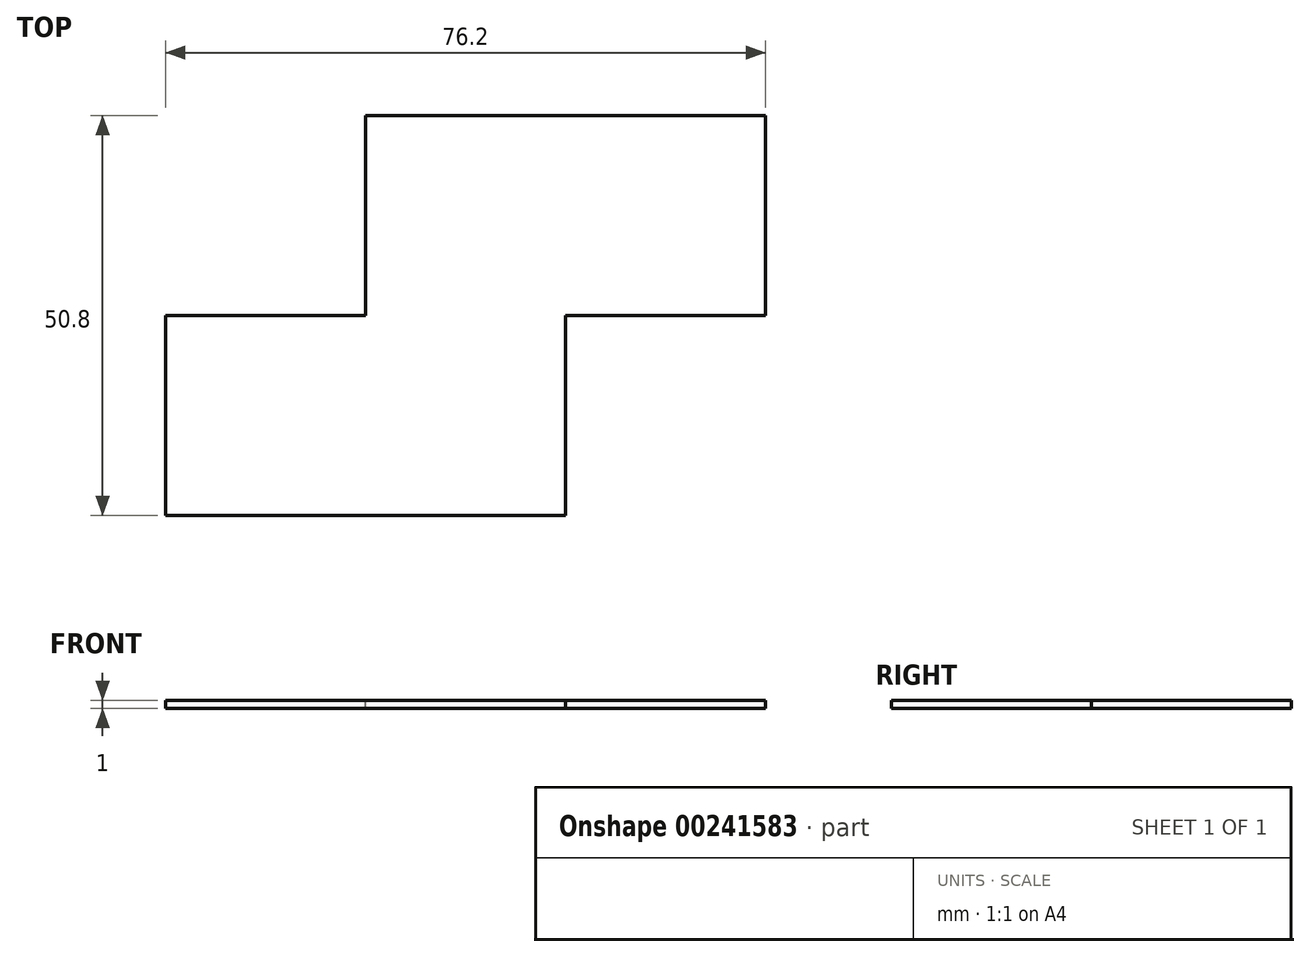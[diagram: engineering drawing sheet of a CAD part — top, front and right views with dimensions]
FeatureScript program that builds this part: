
annotation { "Feature Type Name" : "Feature", "Feature Type Description" : "" }
export const myFeature = defineFeature(function(context is Context, id is Id, definition is map)
    precondition{}
    {
        {
            assignVariable(context, id + "F0", {"name" : "x", "anyValue" : 1});
        }
        {
            var Q0;
            Q0=qCreatedBy(makeId("Top.planeOp"),FACE);
            var sketch = newSketch(context, id + "F1", { "sketchPlane" : qUnion([Q0])});
            skLineSegment(sketch, "E0.bottom", {"start": v(38.1, 25.4) * mm, "end": v(-38.1, 25.4) * mm});
            skLineSegment(sketch, "E0.top", {"start": v(38.1, -25.4) * mm, "end": v(-38.1, -25.4) * mm});
            skLineSegment(sketch, "E0.left", {"start": v(38.1, 25.4) * mm, "end": v(38.1, -25.4) * mm});
            skLineSegment(sketch, "E0.right", {"start": v(-38.1, 25.4) * mm, "end": v(-38.1, -25.4) * mm});
            skPoint(sketch, "E0.middle", {"position": v(0, 0) * mm});
            skSolve(sketch);
        }
        {
            var Q0;
            Q0 = qSketchRegion(id + "F1", true);
            extrude(context, id + "F2", {"entities" : qUnion([Q0]), "depth" : (getVariable(context, 'x')) * mm});
        }
        {
            var Q0;
            Q0=makeQuery(id+"F2.opExtrude","CAP_FACE",FACE,{"disambiguationData":[OSD([sQuery(id+"F1.wireOp",EDGE,"E0.bottom"),sQuery(id+"F1.wireOp",EDGE,"E0.top"),sQuery(id+"F1.wireOp",EDGE,"E0.left"),sQuery(id+"F1.wireOp",EDGE,"E0.right")])],"isStart":false});
            var sketch = newSketch(context, id + "F3", { "sketchPlane" : qUnion([Q0])});
            skLineSegment(sketch, "E1.bottom", {"start": v(-38.1, 25.4) * mm, "end": v(-12.7, 25.4) * mm});
            skLineSegment(sketch, "E1.top", {"start": v(-38.1, 0) * mm, "end": v(-12.7, 0) * mm});
            skLineSegment(sketch, "E1.left", {"start": v(-38.1, 25.4) * mm, "end": v(-38.1, 0) * mm});
            skLineSegment(sketch, "E1.right", {"start": v(-12.7, 25.4) * mm, "end": v(-12.7, 0) * mm});
            skSolve(sketch);
        }
        {
            var Q0;
            Q0=makeQuery(id+"F3.imprint","IMPRINT",FACE,{"disambiguationData":[TD([[makeQuery(id+"F3.imprint","IMPRINT",EDGE,{"derivedFrom":sQuery(id+"F3.wireOp",EDGE,"E1.bottom")}),1.0]])]});
            extrude(context, id + "F4", {"entities" : qUnion([Q0]), "operationType" : NewBodyOperationType.REMOVE, "oppositeDirection" : true, "depth" : (getVariable(context, 'x')) * mm});
        }
        {
            var Q0;
            Q0=makeQuery(id+"F2.opExtrude","CAP_FACE",FACE,{"disambiguationData":[OSD([sQuery(id+"F1.wireOp",EDGE,"E0.bottom"),sQuery(id+"F1.wireOp",EDGE,"E0.top"),sQuery(id+"F1.wireOp",EDGE,"E0.left"),sQuery(id+"F1.wireOp",EDGE,"E0.right")])],"isStart":false});
            var sketch = newSketch(context, id + "F5", { "sketchPlane" : qUnion([Q0])});
            skLineSegment(sketch, "E2.bottom", {"start": v(38.1, -25.4) * mm, "end": v(12.7, -25.4) * mm});
            skLineSegment(sketch, "E2.top", {"start": v(38.1, 0) * mm, "end": v(12.7, 0) * mm});
            skLineSegment(sketch, "E2.left", {"start": v(38.1, -25.4) * mm, "end": v(38.1, 0) * mm});
            skLineSegment(sketch, "E2.right", {"start": v(12.7, -25.4) * mm, "end": v(12.7, 0) * mm});
            skSolve(sketch);
        }
        {
            var Q0;
            Q0=makeQuery(id+"F5.imprint","IMPRINT",FACE,{"disambiguationData":[TD([[makeQuery(id+"F5.imprint","IMPRINT",EDGE,{"derivedFrom":sQuery(id+"F5.wireOp",EDGE,"E2.bottom")}),-1.0]])]});
            extrude(context, id + "F6", {"entities" : qUnion([Q0]), "operationType" : NewBodyOperationType.REMOVE, "oppositeDirection" : true, "depth" : (getVariable(context, 'x')) * mm});
        }
    });
